# Revit family: Magnuson-Valuta-Laminate_L_VA1814L-1
name_source: partatom
category: Furniture
units: mm (PartAtom-declared; Revit-internal decimal feet)

## family parameters
Always vertical = Yes
Cut with Voids When Loaded = No
Room Calculation Point = No
Shared = No
Work Plane-Based = No

## types (1)
- L-VA1814L
    Acrylic Finish = MAG - Acrylic
    Assembly Code = E2020200
    Base Finish = MAG - Anodized Black
    Body Finish = MAG - Oak
    Cost = 0 $
    Default Elevation = 0"
    Depth = 18"
    Description = Laminate 32 gallon body receptacle with internal rigid liner and front access opening.
    Door Finish = MAG - Oak
    Glide Finish = MAG - Plastic Black
    Height = 34"
    Keynote = 12500
    Liner Finish = MAG - Plastic Black
    Magnetic Finish = MAG - Plastic Black
    Manufacturer = Magnuson Group
    Model = L-VA1814L
    Permanent Finish = MAG - Plastic Black
    Product Documentation Link = www.magnusongroup.com
    Pull Finish = MAG - Anodized Silver
    Revit File Built By = https://servex-us.com
    Support Finish = MAG - Anodized Black
    Sustainability = https://magnusongroup.com
    Top Finish = MAG - Anodized Silver
    Type Comments = Valuta
    URL = www.magnusongroup.com
    Width = 14"

## geometry (parser evidence)
native form markers: Sweep x6
no freeform markers — native parametric forms only
